# Revit family: Pump_Heavy_Duty-Solid_Handling-Zoeller-61_HD_4_Inch_Horizontal_Series
name_source: partatom
category: Mechanical Equipment
units: mm (PartAtom-declared; Revit-internal decimal feet)

## family parameters
Always vertical = No
Cut with Voids When Loaded = No
OmniClass Number = 23.60.30.21
OmniClass Title = Pumps
Part Type = Normal
Room Calculation Point = No
Round Connector Dimension = Use Radius
Shared = Yes
Work Plane-Based = Yes

## types (6) — shared parameters
Assembly Code = D2010900
Connecter Description = 4" NPT
Default Elevation = 0"
Description = Commercial Effluent Pumps
Discharge Radius = 2"
Finish = Cast Iron-Zoeller-Powder Coated Epoxy
Flange = ANSI B16.1
Height = 29 1/4"
Hertz = 60
Impeller Type (Default) = Ductile Iron Semi-Open
Impeller Type (Optional) Bronze Semi-open = No
Impeller Type (Optional) Ductile Iron Vortex = No
Installation Type = Floor Mounted
Insulation = Class F
Lead Wires Insulation = Class F
Length = 17 5/16"
Manufacturer = Zoeller
Material = Cast Iron-Zoeller-Powder Coated Epoxy
Max. Stator Temp. = 311 °F
Max. Water Temp. = 104 °F
Mechanical Seals = Tandem carbon/ceramic upper and silicon carbide/silicon carbide lower
Min. Recommended Fluid Level = 24"
Moisture Sensor (Optional) = Moisture Sensing Probes (Requires a circuit in control panel)
Motor Design Letter = NEMA B
Motor Shaft = 416 S.S.
Motor Thermal Shutoff (Single Phase Only) = Thermal Sensors With Automatic Reset
Motor Type = Standard Submersible
O-Rings and Cover Gasket = Buna-N
Operation = Non-Automatic
Phase = 1 or 3
Power Cord = #12-4 SO (Models with a FLA greater than 20 amps use #8-4 gauge power cord)
Price = Prices may vary. Please consult Manufacturer Representative for most up-to-date price list.
Product Documentation Link = https://www.zoellerengineered.com
Product Page URL = https://www.zoellerengineered.com
RPM = 1750
Shaft Seal Lower (Options) = Carbon/Silicon Carbide, Silicon Carbide/Silicon Carbide
Shaft Seal Upper (Options) = Silicon Carbide/Carbon, Silicon Carbide/Silicon Carbide
Shaft Seal Upper Standard = Carbon/Ceramic
Shipping Weight = 245 lbs (111 kg)
Solid Size = 2 1/2" (64 mm)
Solid Size (Optional) 3" = No
Tandem Seals = Standard
Type = Permanent Split Capacitor or 3 Phase
Type SOW Power Cord Length = 300"
URL = https://www.zoellerengineered.com
Void Visibility = -8 17/32"
Warranty Information = 36 Months (Limited)
Waste Connection = Yes
Width = 12 5/8"

## per-type parameters (varying)
| type | Discharge Diameter | Dry Pit (1-3 BHP, Intermittent Duty) | Full Load Amps (Voltage Dependent) | High Temp (1-3 BHP Only) | Impeller Diameter | Inverter Duty Submersible (1-5 BHP Only) | Locked Rotor Amps (Voltage Dependant) | Maximum KW Input | Model | Motor | NEC Locked Rotor Code | Service Factor | Voltage |
| 6120-4" | 4 | Yes | 1.6 - 6.9 | Yes | 4 7/8" | Yes | 11.5 - 48.0 | 1.4 | 6120-4" | 1.0 BHP | M | 1.2 | 200 / 230 / 460 |
| 6121-4" | 4 | Yes | 2.0 - 8.9 | Yes | 5 3/8" | Yes | 11.5 - 48.0 | 1.9 | 6121-4" | 1.5 BHP | J | 1.2 | 200 / 230 / 460 |
| 6122-4" | 4" | Yes | 2.7 - 14.5 | Yes | 5 3/4" | Yes | 16.5 - 86.0 | 2.4 | 6122-4" | 2.0 BHP | K | 1.2 | 200 / 230 / 460 / 575 |
| 6123-4" | 4" | Yes | 3.9 - 17.0 | Yes | 6 3/8" | Yes | 16.2 - 86.0 | 3.5 | 6123-3" | 3.0 BHP | F | 1.2 | 200 / 230 / 460 / 575 |
| 6124-4" | 4" | No | 6.1 - 28.0 | No | 7" | Yes | 23.0 - 139.0 | 5.5 | 6124-4" | 5.0 BHP | E | 1.2 | 200 / 230 / 460 / 575 |
| 6125-4" | 4" | No | 9.0 - 25.3 | No | 7 1/2" | No | 29.0 - 83.0 | 6.9 | 6125-4" | 7.5 BHP | C | 1.0 | 200 / 230 / 460 / 575 |

## geometry (parser evidence)
native form markers: Sweep x1
no freeform markers — native parametric forms only
